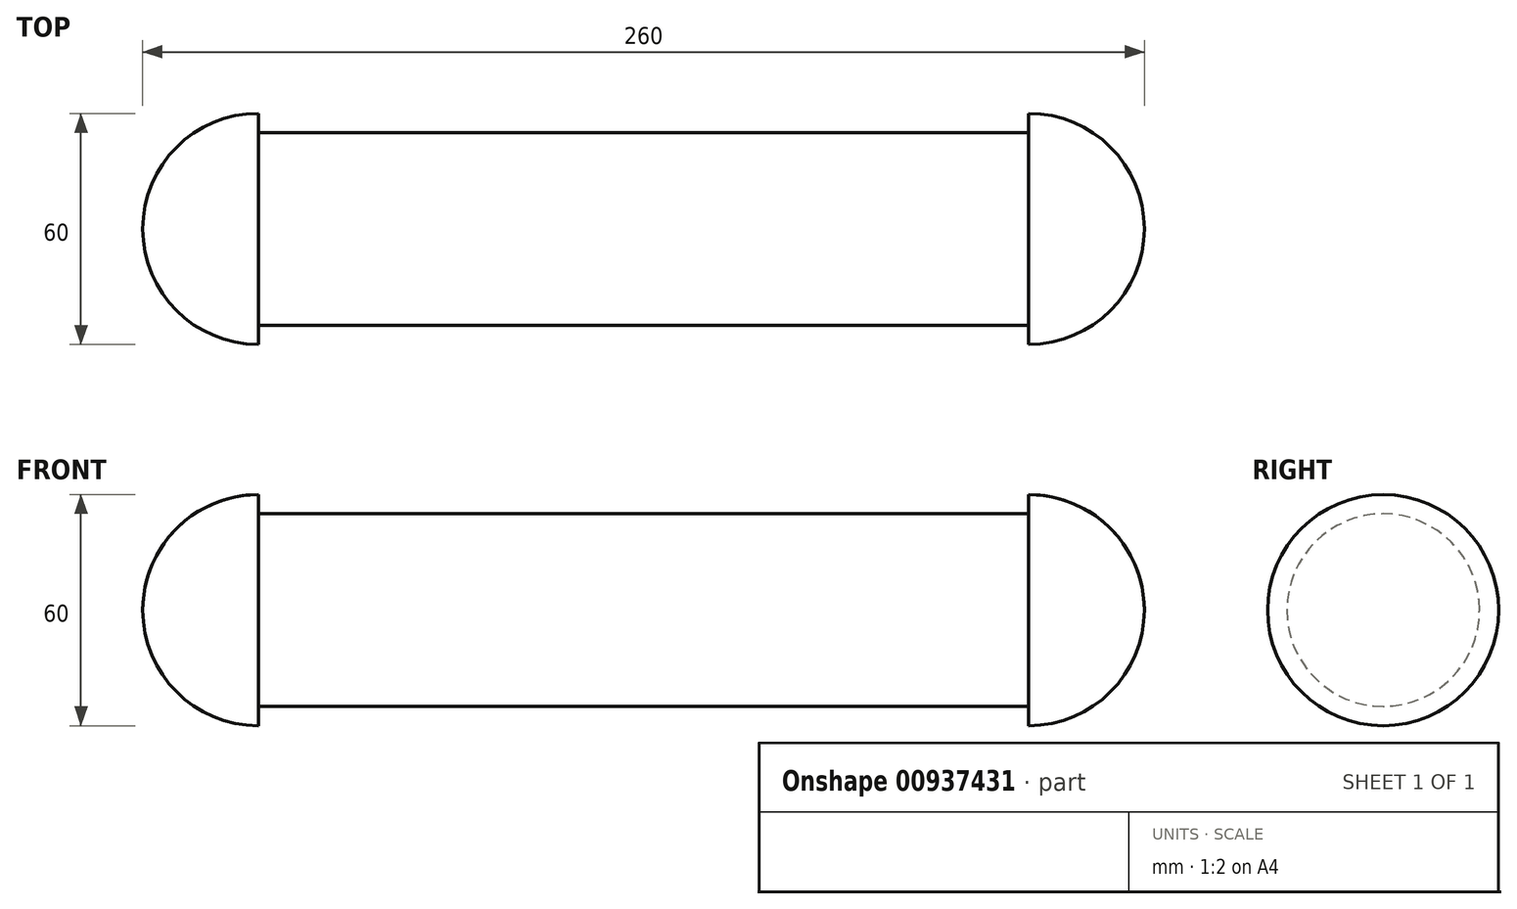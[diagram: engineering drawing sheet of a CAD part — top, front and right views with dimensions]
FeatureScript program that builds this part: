
annotation { "Feature Type Name" : "Feature", "Feature Type Description" : "" }
export const myFeature = defineFeature(function(context is Context, id is Id, definition is map)
    precondition{}
    {
        {
            var Q0;
            Q0=qCreatedBy(makeId("Front.planeOp"),FACE);
            var sketch = newSketch(context, id + "F0", { "sketchPlane" : qUnion([Q0])});
            skLineSegment(sketch, "E0.bottom", {"start": v(-100, 25) * mm, "end": v(100, 25) * mm});
            skLineSegment(sketch, "E0.top", {"start": v(-100, -25) * mm, "end": v(100, -25) * mm});
            skLineSegment(sketch, "E0.left", {"start": v(-100, 25) * mm, "end": v(-100, -25) * mm});
            skLineSegment(sketch, "E0.right", {"start": v(100, 25) * mm, "end": v(100, -25) * mm});
            skPoint(sketch, "E0.middle", {"position": v(0, 0) * mm});
            skLineSegment(sketch, "E1", {"start": v(-100, 0) * mm, "end": v(100, 0) * mm});
            skLineSegment(sketch, "E2", {"start": v(-100, 25) * mm, "end": v(-100, 30) * mm});
            skLineSegment(sketch, "E3", {"start": v(100, 25) * mm, "end": v(100, 30) * mm});
            skLineSegment(sketch, "E4", {"start": v(100, -25) * mm, "end": v(100, -30) * mm});
            skLineSegment(sketch, "E5", {"start": v(-100, -25) * mm, "end": v(-100, -30) * mm});
            skArc(sketch, "E6", {"start": v(100, -30) * mm, "mid": v(130, 0) * mm, "end": v(100, 30) * mm});
            skArc(sketch, "E7", {"start": v(-100, 30) * mm, "mid": v(-130, 0) * mm, "end": v(-100, -30) * mm});
            skLineSegment(sketch, "E8", {"start": v(100, 0) * mm, "end": v(130, 0) * mm});
            skLineSegment(sketch, "E9", {"start": v(-100, 0) * mm, "end": v(-130, 0) * mm});
            skSolve(sketch);
        }
        {
            var Q0;
            {var subQ0=sQuery(id+"F0.wireOp",EDGE,"E3");Q0=makeQuery(id+"F0.imprint","IMPRINT",FACE,{"disambiguationData":[TD([[makeQuery(id+"F0.imprint","IMPRINT",EDGE,{"derivedFrom":subQ0}),-1.0]])]});}
            var Q1;
            {var subQ0=sQuery(id+"F0.wireOp",EDGE,"E0.bottom");Q1=makeQuery(id+"F0.imprint","IMPRINT",FACE,{"disambiguationData":[TD([[makeQuery(id+"F0.imprint","IMPRINT",EDGE,{"derivedFrom":subQ0}),-1.0]])]});}
            var Q2;
            {var subQ0=sQuery(id+"F0.wireOp",EDGE,"E2");Q2=makeQuery(id+"F0.imprint","IMPRINT",FACE,{"disambiguationData":[TD([[makeQuery(id+"F0.imprint","IMPRINT",EDGE,{"derivedFrom":subQ0}),1.0]])]});}
            var Q3;
            Q3=sQuery(id+"F0.wireOp",EDGE,"E1");
            revolve(context, id + "F1", {"surfaceOperationType" : NewSurfaceOperationType.NEW, "entities" : qUnion([Q0, Q1, Q2]), "axis" : qUnion([Q3]), "revolveType" : RevolveType.FULL});
        }
    });
